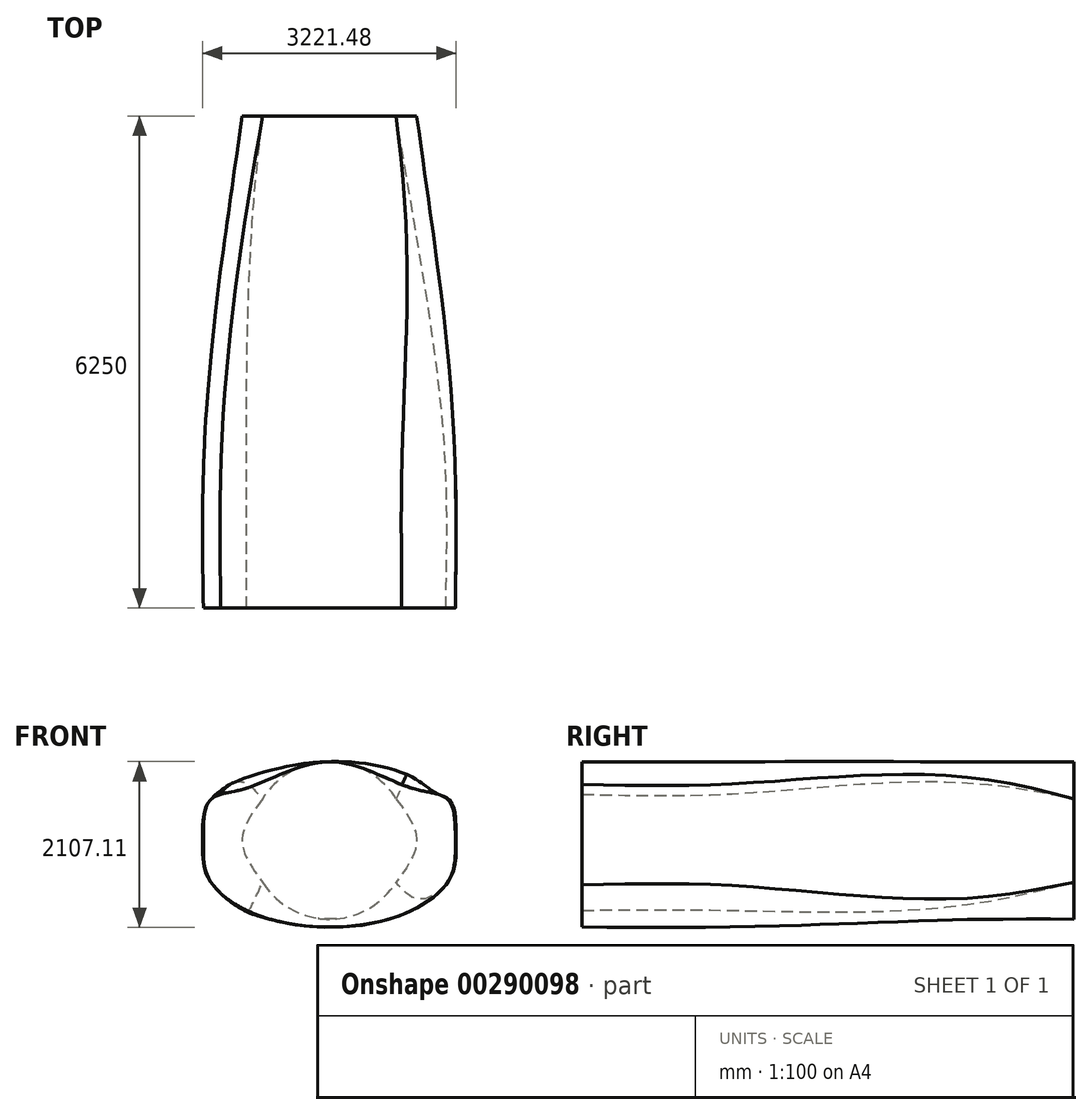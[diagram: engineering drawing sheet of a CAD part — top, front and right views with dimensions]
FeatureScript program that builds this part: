
annotation { "Feature Type Name" : "Feature", "Feature Type Description" : "" }
export const myFeature = defineFeature(function(context is Context, id is Id, definition is map)
    precondition{}
    {
        {
            var Q0;
            Q0=qCreatedBy(makeId("Front.planeOp"),FACE);
            var sketch = newSketch(context, id + "F0", { "sketchPlane" : qUnion([Q0])});
            skPoint(sketch, "E0.middle", {"position": v(0, 0) * mm});
            skFitSpline(sketch, "E1", {"points": [v(0, 1000) * mm, v(1060, 662.5) * mm, v(1517.6, 506.84) * mm, v(1600, 0) * mm, v(1517.6, -506.84) * mm, v(750, -1000) * mm, v(-750, -1000) * mm, v(-1517.6, -506.84) * mm, v(-1600, 0) * mm, v(-1517.6, 506.84) * mm, v(-1060, 662.5) * mm, v(0, 1000) * mm]});
            skSolve(sketch);
        }
        {
            var Q0;
            Q0=qCreatedBy(makeId("Front.planeOp"),FACE);
            cPlane(context, id + "F1", {"entities" : qUnion([Q0]), "cplaneType" : CPlaneType.OFFSET, "offset" : 1750 * mm, "width" : 150 * mm, "height" : 150 * mm});
        }
        {
            var Q0;
            Q0=qCreatedBy(id+"F1.planeOp",FACE);
            var sketch = newSketch(context, id + "F2", { "sketchPlane" : qUnion([Q0])});
            skPoint(sketch, "E2.middle", {"position": v(0, 0) * mm});
            skFitSpline(sketch, "E3", {"points": [v(0, 1000) * mm, v(1060, 662.5) * mm, v(1517.6, 506.84) * mm, v(1600, 0) * mm, v(1517.6, -506.84) * mm, v(750, -1000) * mm, v(-750, -1000) * mm, v(-1517.6, -506.84) * mm, v(-1600, 0) * mm, v(-1517.6, 506.84) * mm, v(-1060, 662.5) * mm, v(0, 1000) * mm]});
            skSolve(sketch);
        }
        {
            var Q0;
            Q0=qCreatedBy(makeId("Front.planeOp"),FACE);
            cPlane(context, id + "F3", {"entities" : qUnion([Q0]), "cplaneType" : CPlaneType.OFFSET, "offset" : 3500 * mm, "oppositeDirection" : true, "width" : 150 * mm, "height" : 150 * mm});
        }
        {
            var Q0;
            Q0=qCreatedBy(id+"F3.planeOp",FACE);
            var sketch = newSketch(context, id + "F4", { "sketchPlane" : qUnion([Q0])});
            skPoint(sketch, "E4.middle", {"position": v(0, 0) * mm});
            skFitSpline(sketch, "E5", {"points": [v(0, 1000) * mm, v(1060, 662.5) * mm, v(1250, 0) * mm, v(1060, -662.5) * mm, v(0, -1000) * mm, v(-1060, -662.5) * mm, v(-1250, 0) * mm, v(-1060, 662.5) * mm, v(0, 1000) * mm]});
            skSolve(sketch);
        }
        {
            var Q0;
            Q0=qCreatedBy(makeId("Front.planeOp"),FACE);
            cPlane(context, id + "F5", {"entities" : qUnion([Q0]), "cplaneType" : CPlaneType.OFFSET, "offset" : 4500 * mm, "oppositeDirection" : true, "width" : 150 * mm, "height" : 150 * mm});
        }
        {
            var Q0;
            Q0=qCreatedBy(id+"F5.planeOp",FACE);
            var sketch = newSketch(context, id + "F6", { "sketchPlane" : qUnion([Q0])});
            skPoint(sketch, "E6.middle", {"position": v(0, 0) * mm});
            skArc(sketch, "E7", {"start": v(848, 530) * mm, "mid": v(0, 1000) * mm, "end": v(-848, 530) * mm});
            skFitSpline(sketch, "E8", {"points": [v(848, 530) * mm, v(1108.5, 0) * mm, v(848, -530) * mm], "startDerivative": vector(781.5, -1060) * mm, "endDerivative": vector(-781.5, -1060) * mm});
            skFitSpline(sketch, "E9", {"points": [v(-848, 530) * mm, v(-1108.5, 0) * mm, v(-848, -530) * mm], "startDerivative": vector(-781.5, -1060) * mm, "endDerivative": vector(781.5, -1060) * mm});
            skArc(sketch, "E10.trimOffspring", {"start": v(-848, -530) * mm, "mid": v(0, -1000) * mm, "end": v(848, -530) * mm});
            skSolve(sketch);
        }
        {
            var Q0;
            Q0=makeQuery(id+"F2.imprint","IMPRINT",FACE,{"disambiguationData":[TD([[makeQuery(id+"F2.imprint","IMPRINT",EDGE,{"derivedFrom":sQuery(id+"F2.wireOp",EDGE,"E3")}),-1.0]])]});
            var Q1;
            Q1=makeQuery(id+"F0.imprint","IMPRINT",FACE,{"disambiguationData":[TD([[makeQuery(id+"F0.imprint","IMPRINT",EDGE,{"derivedFrom":sQuery(id+"F0.wireOp",EDGE,"E1")}),-1.0]])]});
            var Q2;
            Q2=makeQuery(id+"F4.imprint","IMPRINT",FACE,{"disambiguationData":[TD([[makeQuery(id+"F4.imprint","IMPRINT",EDGE,{"derivedFrom":sQuery(id+"F4.wireOp",EDGE,"E5")}),-1.0]])]});
            var Q3;
            Q3=makeQuery(id+"F6.imprint","IMPRINT",FACE,{"disambiguationData":[TD([[makeQuery(id+"F6.imprint","IMPRINT",EDGE,{"derivedFrom":sQuery(id+"F6.wireOp",EDGE,"E7")}),1.0]])]});
            loft(context, id + "F7", {"sheetProfilesArray" : [{ "sheetProfileEntities" : qUnion([Q0]) }, { "sheetProfileEntities" : qUnion([Q1]) }, { "sheetProfileEntities" : qUnion([Q2]) }, { "sheetProfileEntities" : qUnion([Q3]) }]});
        }
    });
